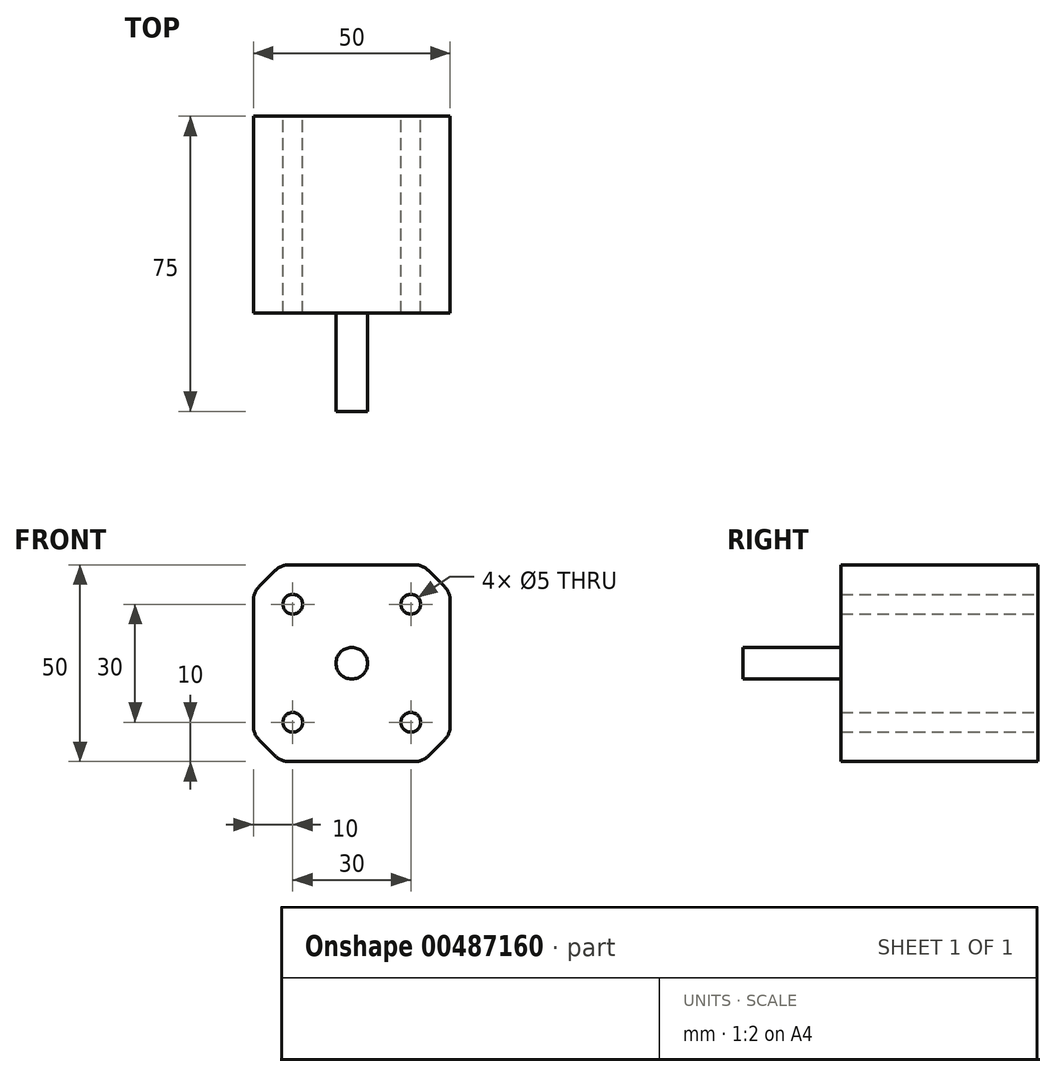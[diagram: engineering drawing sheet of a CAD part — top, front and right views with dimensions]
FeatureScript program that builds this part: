
annotation { "Feature Type Name" : "Feature", "Feature Type Description" : "" }
export const myFeature = defineFeature(function(context is Context, id is Id, definition is map)
    precondition{}
    {
        {
            var Q0;
            Q0=qCreatedBy(makeId("Front.planeOp"),FACE);
            var sketch = newSketch(context, id + "F0", { "sketchPlane" : qUnion([Q0])});
            skLineSegment(sketch, "E0.bottom", {"start": v(-25, 25) * mm, "end": v(25, 25) * mm});
            skLineSegment(sketch, "E0.top", {"start": v(-25, -25) * mm, "end": v(25, -25) * mm});
            skLineSegment(sketch, "E0.left", {"start": v(-25, 25) * mm, "end": v(-25, -25) * mm});
            skLineSegment(sketch, "E0.right", {"start": v(25, 25) * mm, "end": v(25, -25) * mm});
            skSolve(sketch);
        }
        {
            var Q0;
            Q0 = qSketchRegion(id + "F0", true);
            extrude(context, id + "F1", {"entities" : qUnion([Q0]), "depth" : 25 * mm, "hasSecondDirection" : true, "secondDirectionOppositeDirection" : true, "secondDirectionDepth" : 25 * mm});
        }
        {
            var Q0;
            Q0=makeQuery(id+"F1.opExtrude","CAP_FACE",FACE,{"disambiguationData":[OSD([sQuery(id+"F0.wireOp",EDGE,"E0.bottom"),sQuery(id+"F0.wireOp",EDGE,"E0.top"),sQuery(id+"F0.wireOp",EDGE,"E0.left"),sQuery(id+"F0.wireOp",EDGE,"E0.right")])],"isStart":false});
            var sketch = newSketch(context, id + "F2", { "sketchPlane" : qUnion([Q0])});
            skCircle(sketch, "E1", {"center": v(0, 0) * mm, "radius": 4 * mm});
            skSolve(sketch);
        }
        {
            var Q0;
            Q0 = qSketchRegion(id + "F2", true);
            extrude(context, id + "F3", {"entities" : qUnion([Q0]), "operationType" : NewBodyOperationType.ADD, "depth" : 25 * mm});
        }
        {
            var Q0;
            Q0=makeQuery(id+"F1.opExtrude","SWEPT_EDGE",EDGE,{"disambiguationData":[OSD([sQuery(id+"F0.wireOp",EDGE,"E0.bottom"),sQuery(id+"F0.wireOp",EDGE,"E0.left")])]});
            var Q1;
            Q1=makeQuery(id+"F1.opExtrude","SWEPT_EDGE",EDGE,{"disambiguationData":[OSD([sQuery(id+"F0.wireOp",EDGE,"E0.bottom"),sQuery(id+"F0.wireOp",EDGE,"E0.right")])]});
            var Q2;
            Q2=makeQuery(id+"F1.opExtrude","SWEPT_EDGE",EDGE,{"disambiguationData":[OSD([sQuery(id+"F0.wireOp",EDGE,"E0.top"),sQuery(id+"F0.wireOp",EDGE,"E0.right")])]});
            var Q3;
            Q3=makeQuery(id+"F1.opExtrude","SWEPT_EDGE",EDGE,{"disambiguationData":[OSD([sQuery(id+"F0.wireOp",EDGE,"E0.top"),sQuery(id+"F0.wireOp",EDGE,"E0.left")])]});
            chamfer(context, id + "F4", {"entities" : qUnion([Q0, Q1, Q2, Q3]), "width" : 7 * mm, "tangentPropagation" : true});
        }
        {
            var Q0;
            {var subQ0=sQuery(id+"F0.wireOp",EDGE,"E0.bottom");Q0=makeQuery(id+"F4.opChamfer","BLEND_EDGE",EDGE,{"blendedFrom":[makeQuery(id+"F1.opExtrude","SWEPT_EDGE",EDGE,{"disambiguationData":[OSD([subQ0,sQuery(id+"F0.wireOp",EDGE,"E0.left")])]}),makeQuery(id+"F1.opExtrude","SWEPT_FACE",FACE,{"disambiguationData":[OSD([subQ0])]})],"blendedInto":[makeQuery(id+"F1.opExtrude","SWEPT_FACE",FACE,{"disambiguationData":[OSD([subQ0])]})]});}
            var Q1;
            {var subQ0=sQuery(id+"F0.wireOp",EDGE,"E0.left");Q1=makeQuery(id+"F4.opChamfer","BLEND_EDGE",EDGE,{"blendedFrom":[makeQuery(id+"F1.opExtrude","SWEPT_EDGE",EDGE,{"disambiguationData":[OSD([sQuery(id+"F0.wireOp",EDGE,"E0.bottom"),subQ0])]}),makeQuery(id+"F1.opExtrude","SWEPT_FACE",FACE,{"disambiguationData":[OSD([subQ0])]})],"blendedInto":[makeQuery(id+"F1.opExtrude","SWEPT_FACE",FACE,{"disambiguationData":[OSD([subQ0])]})]});}
            var Q2;
            {var subQ0=sQuery(id+"F0.wireOp",EDGE,"E0.bottom");Q2=makeQuery(id+"F4.opChamfer","BLEND_EDGE",EDGE,{"blendedFrom":[makeQuery(id+"F1.opExtrude","SWEPT_EDGE",EDGE,{"disambiguationData":[OSD([subQ0,sQuery(id+"F0.wireOp",EDGE,"E0.right")])]}),makeQuery(id+"F1.opExtrude","SWEPT_FACE",FACE,{"disambiguationData":[OSD([subQ0])]})],"blendedInto":[makeQuery(id+"F1.opExtrude","SWEPT_FACE",FACE,{"disambiguationData":[OSD([subQ0])]})]});}
            var Q3;
            {var subQ0=sQuery(id+"F0.wireOp",EDGE,"E0.right");Q3=makeQuery(id+"F4.opChamfer","BLEND_EDGE",EDGE,{"blendedFrom":[makeQuery(id+"F1.opExtrude","SWEPT_EDGE",EDGE,{"disambiguationData":[OSD([sQuery(id+"F0.wireOp",EDGE,"E0.bottom"),subQ0])]}),makeQuery(id+"F1.opExtrude","SWEPT_FACE",FACE,{"disambiguationData":[OSD([subQ0])]})],"blendedInto":[makeQuery(id+"F1.opExtrude","SWEPT_FACE",FACE,{"disambiguationData":[OSD([subQ0])]})]});}
            var Q4;
            {var subQ0=sQuery(id+"F0.wireOp",EDGE,"E0.right");Q4=makeQuery(id+"F4.opChamfer","BLEND_EDGE",EDGE,{"blendedFrom":[makeQuery(id+"F1.opExtrude","SWEPT_EDGE",EDGE,{"disambiguationData":[OSD([sQuery(id+"F0.wireOp",EDGE,"E0.top"),subQ0])]}),makeQuery(id+"F1.opExtrude","SWEPT_FACE",FACE,{"disambiguationData":[OSD([subQ0])]})],"blendedInto":[makeQuery(id+"F1.opExtrude","SWEPT_FACE",FACE,{"disambiguationData":[OSD([subQ0])]})]});}
            var Q5;
            {var subQ0=sQuery(id+"F0.wireOp",EDGE,"E0.top");Q5=makeQuery(id+"F4.opChamfer","BLEND_EDGE",EDGE,{"blendedFrom":[makeQuery(id+"F1.opExtrude","SWEPT_EDGE",EDGE,{"disambiguationData":[OSD([subQ0,sQuery(id+"F0.wireOp",EDGE,"E0.right")])]}),makeQuery(id+"F1.opExtrude","SWEPT_FACE",FACE,{"disambiguationData":[OSD([subQ0])]})],"blendedInto":[makeQuery(id+"F1.opExtrude","SWEPT_FACE",FACE,{"disambiguationData":[OSD([subQ0])]})]});}
            var Q6;
            {var subQ0=sQuery(id+"F0.wireOp",EDGE,"E0.top");Q6=makeQuery(id+"F4.opChamfer","BLEND_EDGE",EDGE,{"blendedFrom":[makeQuery(id+"F1.opExtrude","SWEPT_EDGE",EDGE,{"disambiguationData":[OSD([subQ0,sQuery(id+"F0.wireOp",EDGE,"E0.left")])]}),makeQuery(id+"F1.opExtrude","SWEPT_FACE",FACE,{"disambiguationData":[OSD([subQ0])]})],"blendedInto":[makeQuery(id+"F1.opExtrude","SWEPT_FACE",FACE,{"disambiguationData":[OSD([subQ0])]})]});}
            var Q7;
            {var subQ0=sQuery(id+"F0.wireOp",EDGE,"E0.left");Q7=makeQuery(id+"F4.opChamfer","BLEND_EDGE",EDGE,{"blendedFrom":[makeQuery(id+"F1.opExtrude","SWEPT_EDGE",EDGE,{"disambiguationData":[OSD([sQuery(id+"F0.wireOp",EDGE,"E0.top"),subQ0])]}),makeQuery(id+"F1.opExtrude","SWEPT_FACE",FACE,{"disambiguationData":[OSD([subQ0])]})],"blendedInto":[makeQuery(id+"F1.opExtrude","SWEPT_FACE",FACE,{"disambiguationData":[OSD([subQ0])]})]});}
            fillet(context, id + "F5", {"entities" : qUnion([Q0, Q1, Q2, Q3, Q4, Q5, Q6, Q7]), "radius" : 5 * mm, "tangentPropagation" : true, "allowEdgeOverflow" : false});
        }
        {
            var Q0;
            Q0=makeQuery(id+"F1.opExtrude","CAP_FACE",FACE,{"disambiguationData":[OSD([sQuery(id+"F0.wireOp",EDGE,"E0.bottom"),sQuery(id+"F0.wireOp",EDGE,"E0.top"),sQuery(id+"F0.wireOp",EDGE,"E0.left"),sQuery(id+"F0.wireOp",EDGE,"E0.right")])],"isStart":true});
            var sketch = newSketch(context, id + "F6", { "sketchPlane" : qUnion([Q0])});
            skCircle(sketch, "E2", {"center": v(-15, 15) * mm, "radius": 2.5 * mm});
            skCircle(sketch, "E3", {"center": v(15, 15) * mm, "radius": 2.5 * mm});
            skCircle(sketch, "E4", {"center": v(15, -15) * mm, "radius": 2.5 * mm});
            skCircle(sketch, "E5", {"center": v(-15, -15) * mm, "radius": 2.5 * mm});
            skSolve(sketch);
        }
        {
            var Q0;
            Q0 = qSketchRegion(id + "F6", true);
            extrude(context, id + "F7", {"entities" : qUnion([Q0]), "operationType" : NewBodyOperationType.REMOVE, "oppositeDirection" : true, "depth" : 50 * mm});
        }
    });
